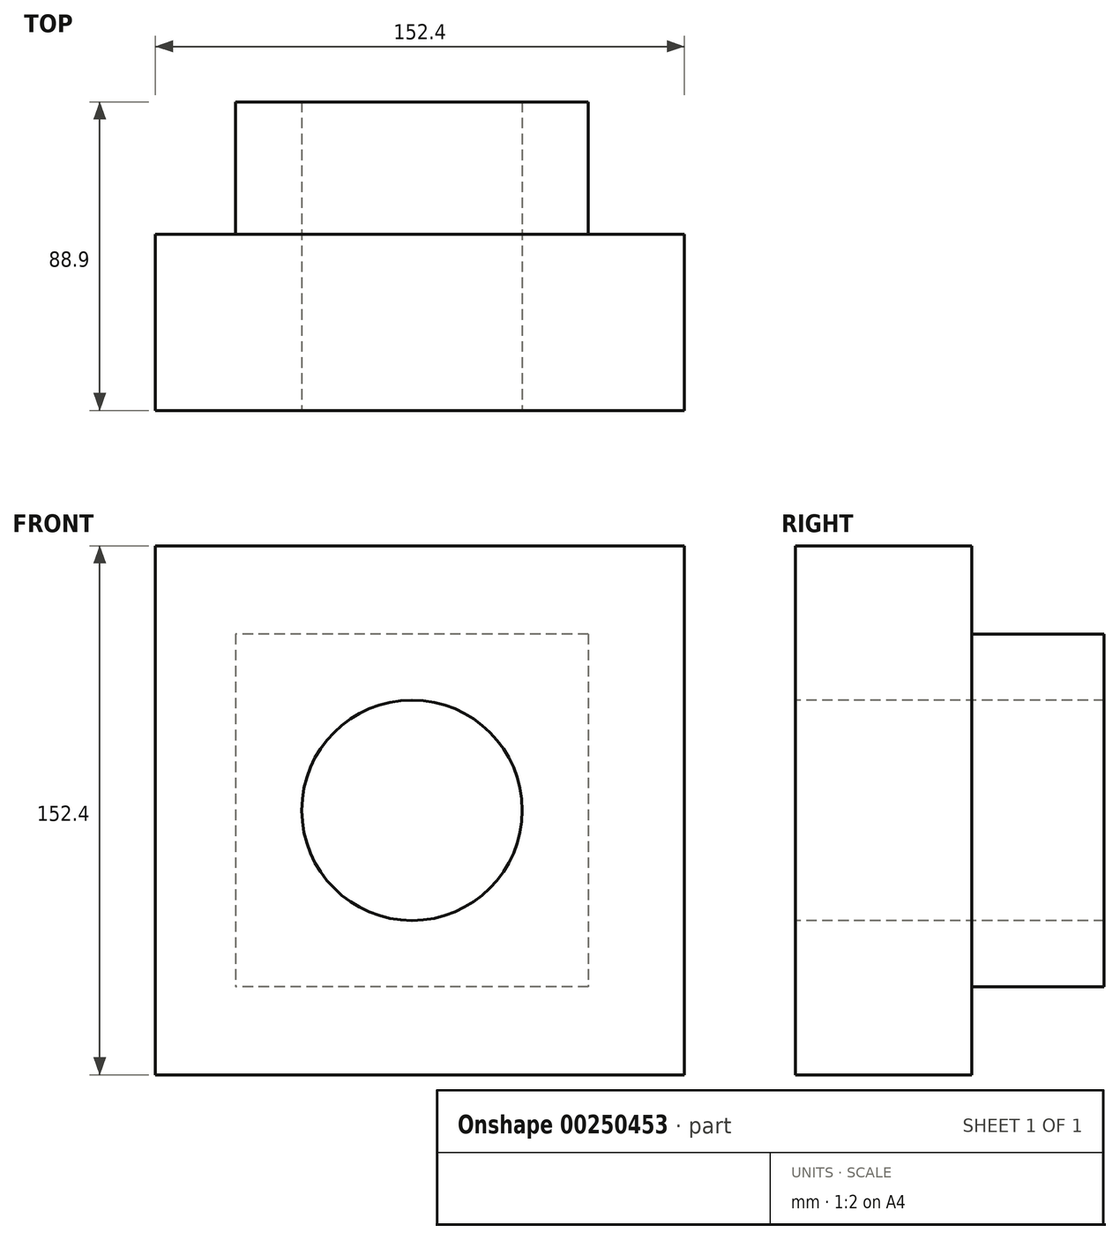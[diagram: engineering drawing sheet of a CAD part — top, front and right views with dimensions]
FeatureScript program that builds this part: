
annotation { "Feature Type Name" : "Feature", "Feature Type Description" : "" }
export const myFeature = defineFeature(function(context is Context, id is Id, definition is map)
    precondition{}
    {
        {
            var Q0;
            Q0=qCreatedBy(makeId("Front.planeOp"),FACE);
            var sketch = newSketch(context, id + "F0", { "sketchPlane" : qUnion([Q0])});
            skCircle(sketch, "E0", {"center": v(0, 0) * mm, "radius": 31.75 * mm});
            skLineSegment(sketch, "E1.bottom", {"start": v(50.8, 50.8) * mm, "end": v(-50.8, 50.8) * mm});
            skLineSegment(sketch, "E1.top", {"start": v(50.8, -50.8) * mm, "end": v(-50.8, -50.8) * mm});
            skLineSegment(sketch, "E1.left", {"start": v(50.8, 50.8) * mm, "end": v(50.8, -50.8) * mm});
            skLineSegment(sketch, "E1.right", {"start": v(-50.8, 50.8) * mm, "end": v(-50.8, -50.8) * mm});
            skLineSegment(sketch, "E2.bottom", {"start": v(78.48, 76.2) * mm, "end": v(-73.92, 76.2) * mm});
            skLineSegment(sketch, "E2.top", {"start": v(78.48, -76.2) * mm, "end": v(-73.92, -76.2) * mm});
            skLineSegment(sketch, "E2.left", {"start": v(78.48, 76.2) * mm, "end": v(78.48, -76.2) * mm});
            skLineSegment(sketch, "E2.right", {"start": v(-73.92, 76.2) * mm, "end": v(-73.92, -76.2) * mm});
            skSolve(sketch);
        }
        {
            var Q0;
            Q0=makeQuery(id+"F0.imprint","IMPRINT",FACE,{"disambiguationData":[TD([[makeQuery(id+"F0.imprint","IMPRINT",EDGE,{"derivedFrom":sQuery(id+"F0.wireOp",EDGE,"E0")}),-1.0]])]});
            extrude(context, id + "F1", {"entities" : qUnion([Q0]), "oppositeDirection" : true, "depth" : 38.1 * mm});
        }
        {
            var Q0;
            Q0=makeQuery(id+"F0.imprint","IMPRINT",FACE,{"disambiguationData":[TD([[makeQuery(id+"F0.imprint","IMPRINT",EDGE,{"derivedFrom":sQuery(id+"F0.wireOp",EDGE,"E1.bottom")}),-1.0]])]});
            var Q1;
            Q1=makeQuery(id+"F0.imprint","IMPRINT",FACE,{"disambiguationData":[TD([[makeQuery(id+"F0.imprint","IMPRINT",EDGE,{"derivedFrom":sQuery(id+"F0.wireOp",EDGE,"E0")}),-1.0]])]});
            extrude(context, id + "F2", {"entities" : qUnion([Q0, Q1]), "operationType" : NewBodyOperationType.ADD, "depth" : 50.8 * mm});
        }
    });
